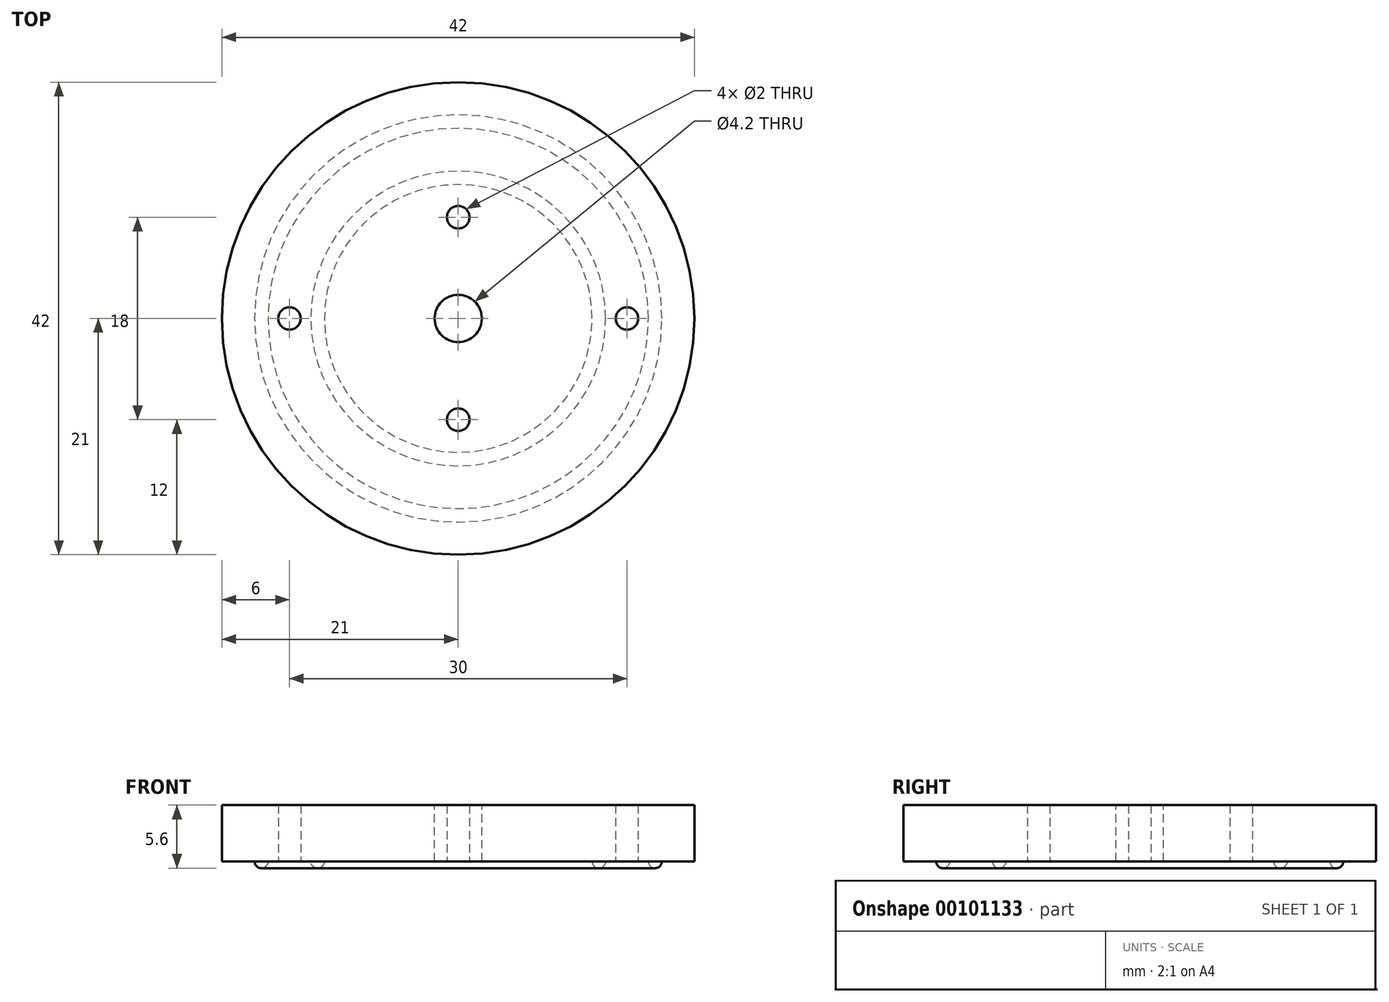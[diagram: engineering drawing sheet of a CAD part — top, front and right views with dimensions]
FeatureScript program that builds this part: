
annotation { "Feature Type Name" : "Feature", "Feature Type Description" : "" }
export const myFeature = defineFeature(function(context is Context, id is Id, definition is map)
    precondition{}
    {
        {
            var Q0;
            Q0=qCreatedBy(makeId("Top.planeOp"),FACE);
            var sketch = newSketch(context, id + "F0", { "sketchPlane" : qUnion([Q0])});
            skCircle(sketch, "E0", {"center": v(0, 0) * mm, "radius": 21 * mm});
            skPoint(sketch, "E1", {"position": v(-15, 0) * mm});
            skPoint(sketch, "E2", {"position": v(15, 0) * mm});
            skPoint(sketch, "E3", {"position": v(0, 9) * mm});
            skPoint(sketch, "E4", {"position": v(0, -9) * mm});
            skSolve(sketch);
        }
        {
            var Q0;
            Q0 = qSketchRegion(id + "F0", true);
            extrude(context, id + "F1", {"entities" : qUnion([Q0]), "depth" : 5 * mm});
        }
        {
            var Q0;
            Q0=sQuery(id+"F0.wireOp",VERTEX,"E3");
            var Q1;
            Q1=sQuery(id+"F0.wireOp",VERTEX,"E2");
            var Q2;
            Q2=sQuery(id+"F0.wireOp",VERTEX,"E4");
            var Q3;
            Q3=sQuery(id+"F0.wireOp",VERTEX,"E1");
            var Q4;
            Q4=makeQuery(id+"F1.opExtrude","SWEPT_BODY",BODY,{"disambiguationData":[OSD([sQuery(id+"F0.wireOp",EDGE,"E0")])]});
            hole(context, id + "F2", {"style" : HoleStyle.SIMPLE, "endStyle" : HoleEndStyle.BLIND, "oppositeDirection" : true, "holeDiameter" : 2 * mm, "holeDepth" : 10 * mm, "locations" : qUnion([Q0, Q1, Q2, Q3]), "scope" : qUnion([Q4])});
        }
        {
            var Q0;
            Q0=makeQuery(id+"F0.imprint","IMPRINT",FACE,{"disambiguationData":[TD([[makeQuery(id+"F0.imprint","IMPRINT",EDGE,{"derivedFrom":sQuery(id+"F0.wireOp",EDGE,"E0")}),1.0]])]});
            var sketch = newSketch(context, id + "F3", { "sketchPlane" : qUnion([Q0])});
            skCircle(sketch, "E5", {"center": v(0, 0) * mm, "radius": 12.5 * mm});
            skSolve(sketch);
        }
        {
            var Q0;
            Q0=qCreatedBy(makeId("Top.planeOp"),FACE);
            var sketch = newSketch(context, id + "F4", { "sketchPlane" : qUnion([Q0])});
            skPoint(sketch, "E6", {"position": v(-12.5, 0) * mm});
            skSolve(sketch);
        }
        {
            var Q0;
            Q0=qCreatedBy(makeId("Front.planeOp"),FACE);
            var sketch = newSketch(context, id + "F5", { "sketchPlane" : qUnion([Q0])});
            skArc(sketch, "E7", {"start": v(-13.1, 0) * mm, "mid": v(-12.5, -0.6) * mm, "end": v(-11.9, 0) * mm});
            skLineSegment(sketch, "E8", {"start": v(-13.1, 0) * mm, "end": v(-11.9, 0) * mm});
            skSolve(sketch);
        }
        {
            var Q0;
            Q0=makeQuery(id+"F5.imprint","IMPRINT",FACE,{"disambiguationData":[TD([[makeQuery(id+"F5.imprint","IMPRINT",EDGE,{"derivedFrom":sQuery(id+"F5.wireOp",EDGE,"E7")}),1.0]])]});
            var Q1;
            Q1=sQuery(id+"F3.wireOp",EDGE,"E5");
            sweep(context, id + "F6", {"operationType" : NewBodyOperationType.ADD, "profiles" : qUnion([Q0]), "path" : qUnion([Q1])});
        }
        {
            var Q0;
            Q0=makeQuery(id+"F1.opExtrude","CAP_FACE",FACE,{"disambiguationData":[OSD([sQuery(id+"F0.wireOp",EDGE,"E0")])],"isStart":false});
            var sketch = newSketch(context, id + "F7", { "sketchPlane" : qUnion([Q0])});
            skCircle(sketch, "E9", {"center": v(0, 0) * mm, "radius": 2.1 * mm});
            skLineSegment(sketch, "E10", {"start": v(-1.79, 1.1) * mm, "end": v(1.79, 1.1) * mm});
            skLineSegment(sketch, "E11", {"start": v(-1.79, -1.1) * mm, "end": v(1.79, -1.1) * mm});
            skSolve(sketch);
        }
        {
            var Q0;
            {var subQ0=sQuery(id+"F7.wireOp",EDGE,"E10");Q0=makeQuery(id+"F7.imprint","IMPRINT",FACE,{"disambiguationData":[TD([[makeQuery(id+"F7.imprint","IMPRINT",EDGE,{"derivedFrom":subQ0}),-1.0]])]});}
            var Q1;
            {var subQ0=sQuery(id+"F7.wireOp",EDGE,"E11");Q1=makeQuery(id+"F7.imprint","IMPRINT",FACE,{"disambiguationData":[TD([[makeQuery(id+"F7.imprint","IMPRINT",EDGE,{"derivedFrom":subQ0}),-1.0]])]});}
            var Q2;
            {var subQ0=sQuery(id+"F7.wireOp",EDGE,"E10");Q2=makeQuery(id+"F7.imprint","IMPRINT",FACE,{"disambiguationData":[TD([[makeQuery(id+"F7.imprint","IMPRINT",EDGE,{"derivedFrom":subQ0}),1.0]])]});}
            extrude(context, id + "F8", {"entities" : qUnion([Q0, Q1, Q2]), "operationType" : NewBodyOperationType.REMOVE, "oppositeDirection" : true, "depth" : 25 * mm});
        }
        {
            var Q0;
            Q0=makeQuery(id+"F0.imprint","IMPRINT",FACE,{"disambiguationData":[TD([[makeQuery(id+"F0.imprint","IMPRINT",EDGE,{"derivedFrom":sQuery(id+"F0.wireOp",EDGE,"E0")}),1.0]])]});
            var sketch = newSketch(context, id + "F9", { "sketchPlane" : qUnion([Q0])});
            skCircle(sketch, "E12", {"center": v(0, 0) * mm, "radius": 17.5 * mm});
            skPoint(sketch, "E13", {"position": v(17.5, 0) * mm});
            skSolve(sketch);
        }
        {
            var Q0;
            Q0=qCreatedBy(makeId("Front.planeOp"),FACE);
            var sketch = newSketch(context, id + "F10", { "sketchPlane" : qUnion([Q0])});
            skArc(sketch, "E14", {"start": v(16.9, 0) * mm, "mid": v(17.5, -0.6) * mm, "end": v(18.1, 0) * mm});
            skLineSegment(sketch, "E15", {"start": v(16.9, 0) * mm, "end": v(18.1, 0) * mm});
            skSolve(sketch);
        }
        {
            var Q0;
            Q0=makeQuery(id+"F10.imprint","IMPRINT",FACE,{"disambiguationData":[TD([[makeQuery(id+"F10.imprint","IMPRINT",EDGE,{"derivedFrom":sQuery(id+"F10.wireOp",EDGE,"E14")}),1.0]])]});
            var Q1;
            Q1=sQuery(id+"F9.wireOp",EDGE,"E12");
            sweep(context, id + "F11", {"operationType" : NewBodyOperationType.ADD, "profiles" : qUnion([Q0]), "path" : qUnion([Q1])});
        }
    });
